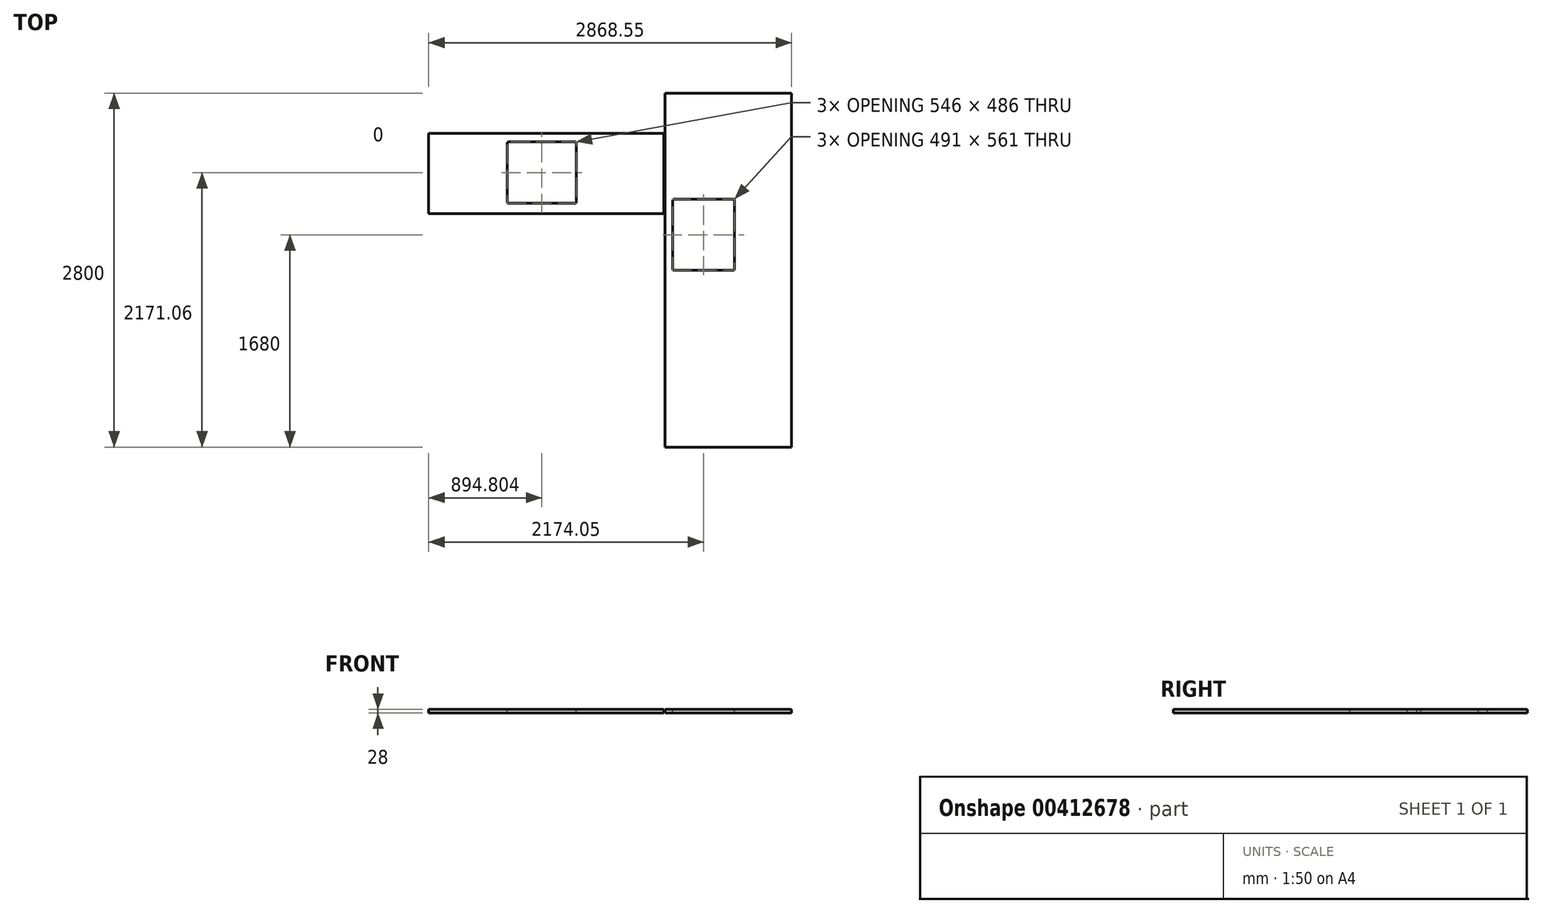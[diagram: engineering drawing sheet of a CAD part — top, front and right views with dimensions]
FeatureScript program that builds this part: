
annotation { "Feature Type Name" : "Feature", "Feature Type Description" : "" }
export const myFeature = defineFeature(function(context is Context, id is Id, definition is map)
    precondition{}
    {
        {
            var Q0;
            Q0=qCreatedBy(makeId("Top.planeOp"),FACE);
            var sketch = newSketch(context, id + "F0", { "sketchPlane" : qUnion([Q0])});
            skLineSegment(sketch, "E0.bottom", {"start": v(-532.97, -323.44) * mm, "end": v(1327.03, -323.44) * mm});
            skLineSegment(sketch, "E0.top", {"start": v(-532.97, 311.56) * mm, "end": v(1327.03, 311.56) * mm});
            skLineSegment(sketch, "E0.left", {"start": v(-532.97, -323.44) * mm, "end": v(-532.97, 311.56) * mm});
            skLineSegment(sketch, "E0.right", {"start": v(1327.03, -323.44) * mm, "end": v(1327.03, 311.56) * mm});
            skSolve(sketch);
        }
        {
            var Q0;
            Q0=makeQuery(id+"F0.imprint","IMPRINT",FACE,{"disambiguationData":[TD([[makeQuery(id+"F0.imprint","IMPRINT",EDGE,{"derivedFrom":sQuery(id+"F0.wireOp",EDGE,"E0.bottom")}),1.0]])]});
            extrude(context, id + "F1", {"entities" : qUnion([Q0]), "depth" : 28 * mm});
        }
        {
            var Q0;
            Q0=qCreatedBy(makeId("Top.planeOp"),FACE);
            var sketch = newSketch(context, id + "F2", { "sketchPlane" : qUnion([Q0])});
            skLineSegment(sketch, "E1.bottom", {"start": v(1335.58, 628.94) * mm, "end": v(2335.58, 628.94) * mm});
            skLineSegment(sketch, "E1.top", {"start": v(1335.58, -2171.06) * mm, "end": v(2335.58, -2171.06) * mm});
            skLineSegment(sketch, "E1.left", {"start": v(1335.58, 628.94) * mm, "end": v(1335.58, -2171.06) * mm});
            skLineSegment(sketch, "E1.right", {"start": v(2335.58, 628.94) * mm, "end": v(2335.58, -2171.06) * mm});
            skSolve(sketch);
        }
        {
            var Q0;
            Q0 = qSketchRegion(id + "F2", true);
            extrude(context, id + "F3", {"entities" : qUnion([Q0]), "depth" : 28 * mm});
        }
        {
            var Q0;
            Q0=makeQuery(id+"F1.opExtrude","CAP_FACE",FACE,{"disambiguationData":[OSD([sQuery(id+"F0.wireOp",EDGE,"E0.bottom"),sQuery(id+"F0.wireOp",EDGE,"E0.top"),sQuery(id+"F0.wireOp",EDGE,"E0.left"),sQuery(id+"F0.wireOp",EDGE,"E0.right")])],"isStart":false});
            var sketch = newSketch(context, id + "F4", { "sketchPlane" : qUnion([Q0])});
            skLineSegment(sketch, "E2.bottom", {"start": v(88.83, 243) * mm, "end": v(634.83, 243) * mm});
            skLineSegment(sketch, "E2.top", {"start": v(88.83, -243) * mm, "end": v(634.83, -243) * mm});
            skLineSegment(sketch, "E2.left", {"start": v(88.83, 243) * mm, "end": v(88.83, -243) * mm});
            skLineSegment(sketch, "E2.right", {"start": v(634.83, 243) * mm, "end": v(634.83, -243) * mm});
            skLineSegment(sketch, "E3", {"start": v(634.83, -323.44) * mm, "end": v(634.83, 311.56) * mm, "construction": true});
            skPoint(sketch, "E4", {"position": v(634.83, 0) * mm});
            skSolve(sketch);
        }
        {
            var Q0;
            Q0=makeQuery(id+"F4.imprint","IMPRINT",FACE,{"disambiguationData":[TD([[makeQuery(id+"F4.imprint","IMPRINT",EDGE,{"derivedFrom":sQuery(id+"F4.wireOp",EDGE,"E2.bottom")}),-1.0]])]});
            extrude(context, id + "F5", {"entities" : qUnion([Q0]), "operationType" : NewBodyOperationType.REMOVE, "endBound" : BoundingType.THROUGH_ALL, "oppositeDirection" : true, "depth" : 25 * mm});
        }
        {
            var Q0;
            Q0=makeQuery(id+"F5.boolean.opBoolean","COPY",EDGE,{"derivedFrom":makeQuery(id+"F5.opExtrude","SWEPT_EDGE",EDGE,{"disambiguationData":[OSD([sQuery(id+"F4.wireOp",EDGE,"E2.bottom"),sQuery(id+"F4.wireOp",EDGE,"E2.right")])]})});
            var Q1;
            Q1=makeQuery(id+"F5.boolean.opBoolean","COPY",EDGE,{"derivedFrom":makeQuery(id+"F5.opExtrude","SWEPT_EDGE",EDGE,{"disambiguationData":[OSD([sQuery(id+"F4.wireOp",EDGE,"E2.top"),sQuery(id+"F4.wireOp",EDGE,"E2.left")])]})});
            var Q2;
            Q2=makeQuery(id+"F5.boolean.opBoolean","COPY",EDGE,{"derivedFrom":makeQuery(id+"F5.opExtrude","SWEPT_EDGE",EDGE,{"disambiguationData":[OSD([sQuery(id+"F4.wireOp",EDGE,"E2.top"),sQuery(id+"F4.wireOp",EDGE,"E2.right")])]})});
            var Q3;
            Q3=makeQuery(id+"F5.boolean.opBoolean","COPY",EDGE,{"derivedFrom":makeQuery(id+"F5.opExtrude","SWEPT_EDGE",EDGE,{"disambiguationData":[OSD([sQuery(id+"F4.wireOp",EDGE,"E2.bottom"),sQuery(id+"F4.wireOp",EDGE,"E2.left")])]})});
            fillet(context, id + "F6", {"entities" : qUnion([Q0, Q1, Q2, Q3]), "radius" : 10 * mm, "tangentPropagation" : true, "allowEdgeOverflow" : false});
        }
        {
            var Q0;
            Q0=makeQuery(id+"F3.opExtrude","CAP_FACE",FACE,{"disambiguationData":[OSD([sQuery(id+"F2.wireOp",EDGE,"E1.bottom"),sQuery(id+"F2.wireOp",EDGE,"E1.top"),sQuery(id+"F2.wireOp",EDGE,"E1.left"),sQuery(id+"F2.wireOp",EDGE,"E1.right")])],"isStart":false});
            var sketch = newSketch(context, id + "F7", { "sketchPlane" : qUnion([Q0])});
            skLineSegment(sketch, "E5", {"start": v(2335.58, -491.06) * mm, "end": v(1335.58, -491.06) * mm, "construction": true});
            skLineSegment(sketch, "E6.bottom", {"start": v(1395.58, -210.56) * mm, "end": v(1886.58, -210.56) * mm});
            skLineSegment(sketch, "E6.top", {"start": v(1395.58, -771.56) * mm, "end": v(1886.58, -771.56) * mm});
            skLineSegment(sketch, "E6.left", {"start": v(1395.58, -210.56) * mm, "end": v(1395.58, -771.56) * mm});
            skLineSegment(sketch, "E6.right", {"start": v(1886.58, -210.56) * mm, "end": v(1886.58, -771.56) * mm});
            skPoint(sketch, "E7", {"position": v(1395.58, -491.06) * mm});
            skLineSegment(sketch, "E8", {"start": v(1729.88, -191.06) * mm, "end": v(1729.88, -791.06) * mm, "construction": true});
            skPoint(sketch, "E9", {"position": v(1729.88, -491.06) * mm});
            skLineSegment(sketch, "E10", {"start": v(1729.88, -191.06) * mm, "end": v(1729.88, 628.94) * mm, "construction": true});
            skSolve(sketch);
        }
        {
            var Q0;
            Q0 = qSketchRegion(id + "F7", true);
            extrude(context, id + "F8", {"entities" : qUnion([Q0]), "operationType" : NewBodyOperationType.REMOVE, "endBound" : BoundingType.THROUGH_ALL, "oppositeDirection" : true, "depth" : 25 * mm});
        }
        {
            var Q0;
            Q0=makeQuery(id+"F8.boolean.opBoolean","COPY",EDGE,{"derivedFrom":makeQuery(id+"F8.opExtrude","SWEPT_EDGE",EDGE,{"disambiguationData":[OSD([sQuery(id+"F7.wireOp",EDGE,"E6.bottom"),sQuery(id+"F7.wireOp",EDGE,"E6.left")])]})});
            var Q1;
            Q1=makeQuery(id+"F8.boolean.opBoolean","COPY",EDGE,{"derivedFrom":makeQuery(id+"F8.opExtrude","SWEPT_EDGE",EDGE,{"disambiguationData":[OSD([sQuery(id+"F7.wireOp",EDGE,"E6.bottom"),sQuery(id+"F7.wireOp",EDGE,"E6.right")])]})});
            var Q2;
            Q2=makeQuery(id+"F8.boolean.opBoolean","COPY",EDGE,{"derivedFrom":makeQuery(id+"F8.opExtrude","SWEPT_EDGE",EDGE,{"disambiguationData":[OSD([sQuery(id+"F7.wireOp",EDGE,"E6.top"),sQuery(id+"F7.wireOp",EDGE,"E6.left")])]})});
            var Q3;
            Q3=makeQuery(id+"F8.boolean.opBoolean","COPY",EDGE,{"derivedFrom":makeQuery(id+"F8.opExtrude","SWEPT_EDGE",EDGE,{"disambiguationData":[OSD([sQuery(id+"F7.wireOp",EDGE,"E6.top"),sQuery(id+"F7.wireOp",EDGE,"E6.right")])]})});
            fillet(context, id + "F9", {"entities" : qUnion([Q0, Q1, Q2, Q3]), "radius" : 10 * mm, "tangentPropagation" : true, "allowEdgeOverflow" : false});
        }
    });
